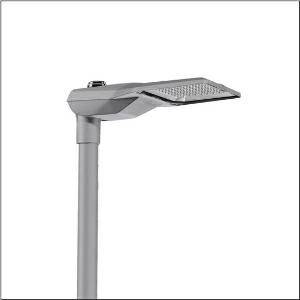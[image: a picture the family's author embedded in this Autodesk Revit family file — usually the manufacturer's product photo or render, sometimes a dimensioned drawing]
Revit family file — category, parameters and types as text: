
# Revit family: streetlight_sl_21_midi___st1_5a_5xe7p47n08lb_54ff
name_source: partatom
category: Lighting Fixtures
units: mm (PartAtom-declared; Revit-internal decimal feet)

## family parameters
Cut with Voids When Loaded = No
Host = Face
Light Source = No
Part Type = Normal
Room Calculation Point = No
Round Connector Dimension = Use Diameter
Shared = No

## types (1)
- --- (1 x LED, 14690 lm, 98.3 W, 4000K)
    Apparent Load = 98 VA
    CIE Flux Codes = 22 53 95 100 100
    Color Rendering = 70
    Color Temperature = 4000K
    Default Elevation = 1800 mm
    Description = Streetlight SL 21 midi, mast luminaire, primary light control with lens, of PMMA, primary optical cover: cover, of toughened safety glass, transparent, light distribution: ST1.5a, light emission: direct distribution, primary light characteristic: asymmetric, installation type: side-entry, LED, 3G 2.5mm², High Power LED, rated luminous flux: 14.690lm, luminous efficacy: 149lm/W, light colour: 740, colour temperature: 4000K, control: overheat protection, presetting dimming linear, constant luminous flux control, time-dependent luminous flux control, flexible luminous flux parameterisation, mains connection: 220..240V, AC, 50/60Hz, connection cable pre-assembled, cable length: 10,5m, wiring characteristics: H05VV-F, start of lifetime: 98W, end of service life: 101W, reduction: 45W, luminaire housing, of diecast aluminium (EN AC-44300), powder-coated, Siteco® metallic grey (DB 702S), corrosivity category C5 mid according to DIN EN ISO 12944, multi-level sealing system, sealing non-destructively replaceable, inclination adjustable: 0°, 5°, 10°, 15°, length: 644mm, width: 335mm, height: 110mm, spigot size: 42mm (side-entry), protection rating (complete): IP66, insulation class (complete): insulation class I (protective earthing), certification: CE, ENEC, ENEC+, VDE, impact resistance: IK09, permissible operating ambient temperature for outdoor applications: -40..+50°C, standard-compliant lighting for roads and squares, packaging unit: 1 piece

Light Distribution: ST1.5a
    Height = 111 mm
    Lamp = 1 x LED
    Lamp Light Flux = 14690 lm
    Lamp Power = 98.3 W
    Lamp count = 1
    Length = 644 mm
    Luminous efficacy = 149 lm/W
    Manufacturer = Siteco
    ModVariant = No
    Model = 5XE7P47N08LB
    Number of Poles = 1
    OnlyDefault = Yes
    Power Factor = 1
    Product Name = Streetlight SL 21 midi | ST1.5a
    Product group = mast luminaire | pylon top
    ProductGroupID = 6100
    Protection Class = Protection class I
    Protection Degree = IP 66
    RLX_Detail_Level = 1
    RLX_Emergency_Light_Flux = 0 lm
    RLX_Emergency_Type = 0
    RLX_Emergency_Type_DB = No
    RlxData = <blob elided: 93853 chars, md5=237371d9>
    Socket = socket
    Standby Power = 0 W
    System Light Flux = 14690 lm
    System Power = 98 W
    Type Comments = factory setting: luminous flux: 100 % | dim-lin: 254 | 1020 mA
    Type Image = l_1294377.jpg
    URL = http://relux.com
    VarID = @adj_082799
    Voltage = 0 V
    Weight = 0.00 kg
    Width = 336 mm

## geometry (parser evidence)
native form markers: Blend x4, Sweep x11
no freeform markers — native parametric forms only
